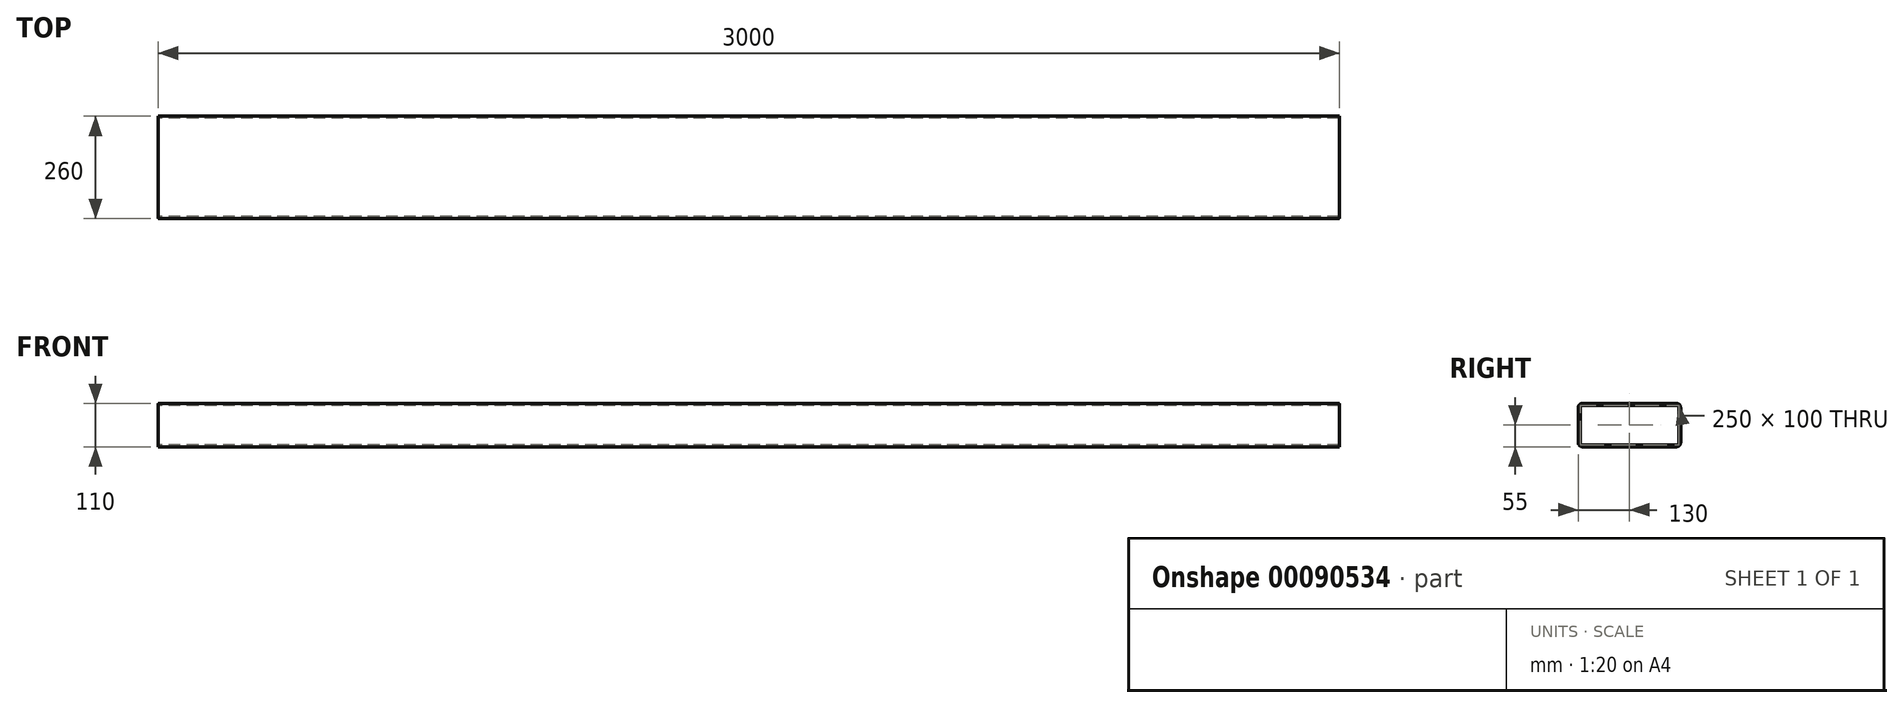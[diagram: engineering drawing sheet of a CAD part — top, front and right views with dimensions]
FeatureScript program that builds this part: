
annotation { "Feature Type Name" : "Feature", "Feature Type Description" : "" }
export const myFeature = defineFeature(function(context is Context, id is Id, definition is map)
    precondition{}
    {
        {
            var Q0;
            Q0=qCreatedBy(makeId("Right.planeOp"),FACE);
            var sketch = newSketch(context, id + "F0", { "sketchPlane" : qUnion([Q0])});
            skLineSegment(sketch, "E0.bottom", {"start": v(125, -50) * mm, "end": v(-125, -50) * mm});
            skLineSegment(sketch, "E0.top", {"start": v(125, 50) * mm, "end": v(-125, 50) * mm});
            skLineSegment(sketch, "E0.left", {"start": v(125, -50) * mm, "end": v(125, 50) * mm});
            skLineSegment(sketch, "E0.right", {"start": v(-125, -50) * mm, "end": v(-125, 50) * mm});
            skPoint(sketch, "E0.middle", {"position": v(0, 0) * mm});
            skLineSegment(sketch, "E1.0", {"start": v(130, 55) * mm, "end": v(-130, 55) * mm});
            skLineSegment(sketch, "E1.1", {"start": v(130, -55) * mm, "end": v(130, 55) * mm});
            skLineSegment(sketch, "E1.2", {"start": v(130, -55) * mm, "end": v(-130, -55) * mm});
            skLineSegment(sketch, "E1.3", {"start": v(-130, -55) * mm, "end": v(-130, 55) * mm});
            skSolve(sketch);
        }
        {
            var Q0;
            Q0 = qSketchRegion(id + "F0", true);
            extrude(context, id + "F1", {"entities" : qUnion([Q0]), "depth" : 3000 * mm});
        }
        {
            var Q0;
            Q0=makeQuery(id+"F1.opExtrude","SWEPT_EDGE",EDGE,{"disambiguationData":[OSD([sQuery(id+"F0.wireOp",EDGE,"E1.0"),sQuery(id+"F0.wireOp",EDGE,"E1.3")])]});
            var Q1;
            Q1=makeQuery(id+"F1.opExtrude","SWEPT_EDGE",EDGE,{"disambiguationData":[OSD([sQuery(id+"F0.wireOp",EDGE,"E1.0"),sQuery(id+"F0.wireOp",EDGE,"E1.1")])]});
            var Q2;
            Q2=makeQuery(id+"F1.opExtrude","SWEPT_EDGE",EDGE,{"disambiguationData":[OSD([sQuery(id+"F0.wireOp",EDGE,"E1.2"),sQuery(id+"F0.wireOp",EDGE,"E1.3")])]});
            var Q3;
            Q3=makeQuery(id+"F1.opExtrude","SWEPT_EDGE",EDGE,{"disambiguationData":[OSD([sQuery(id+"F0.wireOp",EDGE,"E1.1"),sQuery(id+"F0.wireOp",EDGE,"E1.2")])]});
            fillet(context, id + "F2", {"entities" : qUnion([Q0, Q1, Q2, Q3]), "radius" : 10 * mm, "tangentPropagation" : true, "allowEdgeOverflow" : false});
        }
    });
